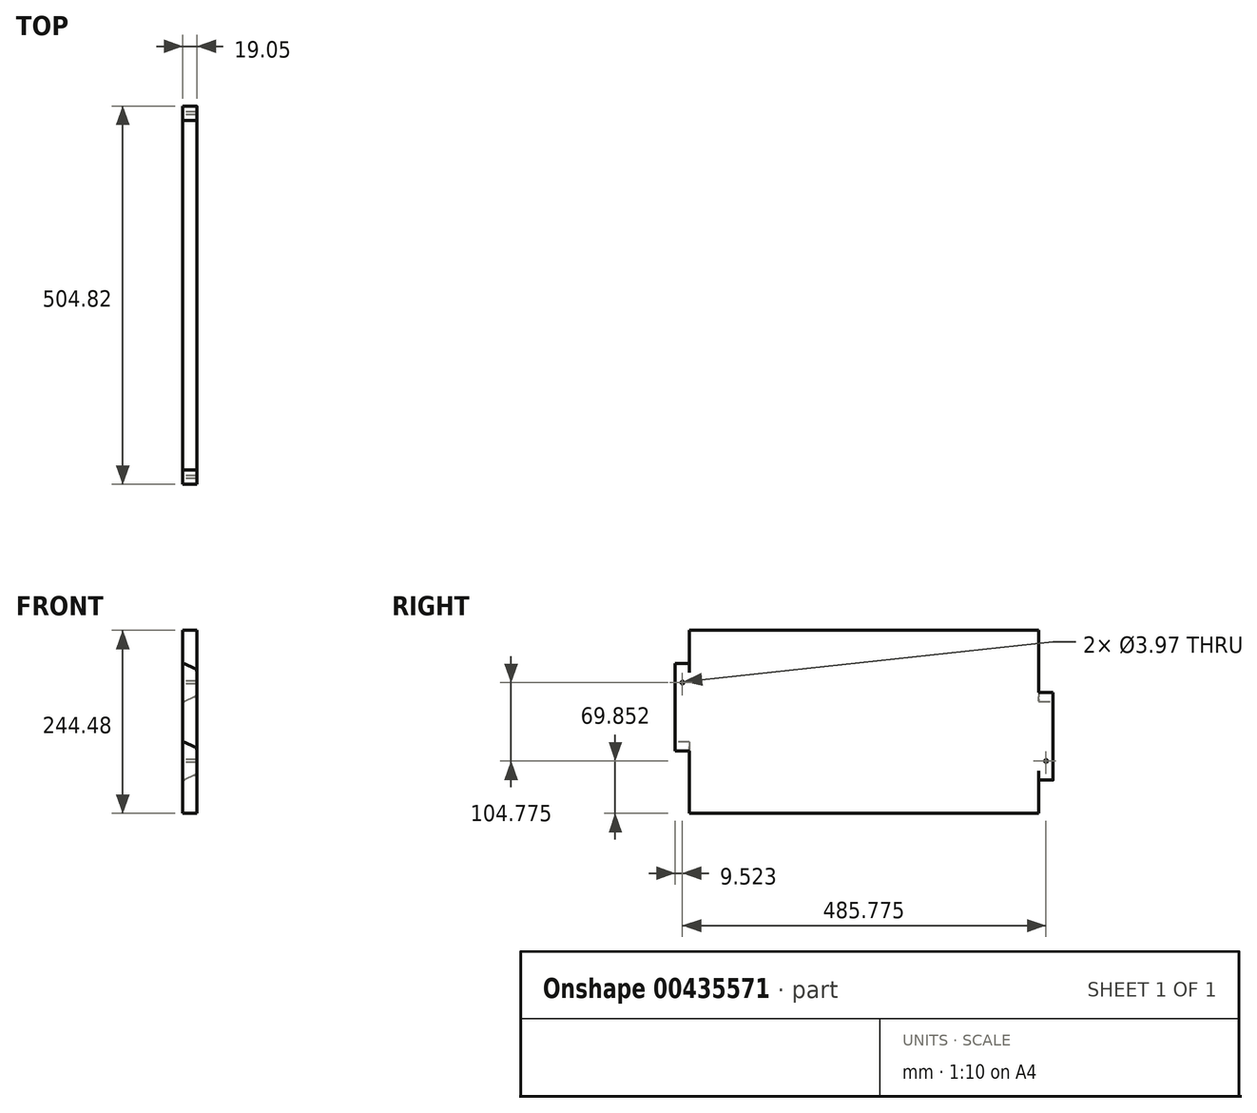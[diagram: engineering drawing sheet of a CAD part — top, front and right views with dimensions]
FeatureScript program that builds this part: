
annotation { "Feature Type Name" : "Feature", "Feature Type Description" : "" }
export const myFeature = defineFeature(function(context is Context, id is Id, definition is map)
    precondition{}
    {
        {
            var Q0;
            Q0=qCreatedBy(makeId("Right.planeOp"),FACE);
            var sketch = newSketch(context, id + "F0", { "sketchPlane" : qUnion([Q0])});
            skLineSegment(sketch, "E0.bottom", {"start": v(252.41, 122.24) * mm, "end": v(-252.41, 122.24) * mm});
            skLineSegment(sketch, "E0.top", {"start": v(252.41, -122.24) * mm, "end": v(-252.41, -122.24) * mm});
            skLineSegment(sketch, "E0.left", {"start": v(252.41, 122.24) * mm, "end": v(252.41, -122.24) * mm});
            skLineSegment(sketch, "E0.right", {"start": v(-252.41, 122.24) * mm, "end": v(-252.41, -122.24) * mm});
            skPoint(sketch, "E0.middle", {"position": v(0, 0) * mm});
            skSolve(sketch);
        }
        {
            var Q0;
            Q0=makeQuery(id+"F0.imprint","IMPRINT",FACE,{"disambiguationData":[TD([[makeQuery(id+"F0.imprint","IMPRINT",EDGE,{"derivedFrom":sQuery(id+"F0.wireOp",EDGE,"E0.bottom")}),1.0]])]});
            extrude(context, id + "F1", {"entities" : qUnion([Q0]), "depth" : 19.05 * mm, "offsetDistance" : 25.4 * mm});
        }
        {
            var Q0;
            Q0=makeQuery(id+"F1.opExtrude","SWEPT_FACE",FACE,{"disambiguationData":[OSD([sQuery(id+"F0.wireOp",EDGE,"E0.right")])]});
            var sketch = newSketch(context, id + "F2", { "sketchPlane" : qUnion([Q0])});
            skLineSegment(sketch, "E1", {"start": v(0, -122.24) * mm, "end": v(0, 122.24) * mm});
            skArc(sketch, "E2.MirrorCS", {"start": v(0.21, -26.99) * mm, "mid": v(1.56, -27.13) * mm, "end": v(2.84, -27.56) * mm});
            skLineSegment(sketch, "E3.MirrorCS", {"start": v(0.21, -77.79) * mm, "end": v(0, -77.79) * mm});
            skArc(sketch, "E4.MirrorCS", {"start": v(2.84, -77.22) * mm, "mid": v(1.56, -77.64) * mm, "end": v(0.21, -77.79) * mm});
            skLineSegment(sketch, "E5.MirrorCS", {"start": v(0, -26.99) * mm, "end": v(0.21, -26.99) * mm});
            skLineSegment(sketch, "E6.MirrorCS", {"start": v(15.33, -71.54) * mm, "end": v(2.84, -77.22) * mm});
            skArc(sketch, "E7.MirrorCS", {"start": v(15.33, -33.23) * mm, "mid": v(18.04, -35.58) * mm, "end": v(19.05, -39.01) * mm});
            skArc(sketch, "E8.MirrorCS", {"start": v(19.05, -65.76) * mm, "mid": v(18.04, -69.2) * mm, "end": v(15.33, -71.54) * mm});
            skLineSegment(sketch, "E9.MirrorCS", {"start": v(19.05, -39.01) * mm, "end": v(19.05, -65.76) * mm});
            skLineSegment(sketch, "E10.MirrorCS", {"start": v(2.84, -27.56) * mm, "end": v(15.33, -33.23) * mm});
            skPoint(sketch, "E11.MirrorP", {"position": v(1.59, -77.79) * mm});
            skPoint(sketch, "E12.MirrorP", {"position": v(19.05, -34.93) * mm});
            skPoint(sketch, "E13.MirrorP", {"position": v(1.59, -26.99) * mm});
            skPoint(sketch, "E14.MirrorP", {"position": v(19.05, -69.85) * mm});
            skLineSegment(sketch, "E15.MirrorCS", {"start": v(0.21, 77.79) * mm, "end": v(0, 77.79) * mm});
            skArc(sketch, "E16.MirrorCS", {"start": v(0.21, 26.99) * mm, "mid": v(1.56, 27.13) * mm, "end": v(2.84, 27.56) * mm});
            skLineSegment(sketch, "E17.MirrorCS", {"start": v(0, 26.99) * mm, "end": v(0.21, 26.99) * mm});
            skArc(sketch, "E18.MirrorCS", {"start": v(2.84, 77.22) * mm, "mid": v(1.56, 77.64) * mm, "end": v(0.21, 77.79) * mm});
            skLineSegment(sketch, "E19.MirrorCS", {"start": v(15.33, 71.54) * mm, "end": v(2.84, 77.22) * mm});
            skArc(sketch, "E20.MirrorCS", {"start": v(15.33, 33.23) * mm, "mid": v(18.04, 35.58) * mm, "end": v(19.05, 39.01) * mm});
            skArc(sketch, "E21.MirrorCS", {"start": v(19.05, 65.76) * mm, "mid": v(18.04, 69.2) * mm, "end": v(15.33, 71.54) * mm});
            skLineSegment(sketch, "E22.MirrorCS", {"start": v(2.84, 27.56) * mm, "end": v(15.33, 33.23) * mm});
            skLineSegment(sketch, "E23.MirrorCS", {"start": v(25.44, 66.94) * mm, "end": v(-6.35, 81.4) * mm, "construction": true});
            skLineSegment(sketch, "E24.MirrorCS", {"start": v(-6.35, 26.99) * mm, "end": v(9.53, 26.99) * mm, "construction": true});
            skLineSegment(sketch, "E25.MirrorCS", {"start": v(9.53, 77.79) * mm, "end": v(-6.35, 77.79) * mm, "construction": true});
            skLineSegment(sketch, "E26.MirrorCS", {"start": v(-6.35, 23.38) * mm, "end": v(25.44, 37.83) * mm, "construction": true});
            skLineSegment(sketch, "E27.MirrorCS", {"start": v(19.05, 39.01) * mm, "end": v(19.05, 65.76) * mm});
            skLineSegment(sketch, "E28.MirrorCS", {"start": v(19.05, 26.99) * mm, "end": v(19.05, 77.79) * mm, "construction": true});
            skPoint(sketch, "E29.MirrorP", {"position": v(1.59, 77.79) * mm});
            skPoint(sketch, "E30.MirrorP", {"position": v(19.05, 34.93) * mm});
            skPoint(sketch, "E31.MirrorP", {"position": v(1.59, 26.99) * mm});
            skLineSegment(sketch, "E32.MirrorCS", {"start": v(0, 20.64) * mm, "end": v(0, 84.14) * mm, "construction": true});
            skPoint(sketch, "E33.MirrorP", {"position": v(19.05, 69.85) * mm});
            skSolve(sketch);
        }
        {
            var Q0;
            Q0=makeQuery(id+"F1.opExtrude","SWEPT_FACE",FACE,{"disambiguationData":[OSD([sQuery(id+"F0.wireOp",EDGE,"E0.left")])]});
            var sketch = newSketch(context, id + "F3", { "sketchPlane" : qUnion([Q0])});
            skLineSegment(sketch, "E34", {"start": v(0, 122.24) * mm, "end": v(0, -122.24) * mm});
            skArc(sketch, "E35.MirrorCS", {"start": v(-0.21, 26.99) * mm, "mid": v(-1.56, 27.13) * mm, "end": v(-2.84, 27.56) * mm});
            skLineSegment(sketch, "E36.MirrorCS", {"start": v(-0.21, 77.79) * mm, "end": v(0, 77.79) * mm});
            skArc(sketch, "E37.MirrorCS", {"start": v(-2.84, 77.22) * mm, "mid": v(-1.56, 77.64) * mm, "end": v(-0.21, 77.79) * mm});
            skLineSegment(sketch, "E38.MirrorCS", {"start": v(0, 26.99) * mm, "end": v(-0.21, 26.99) * mm});
            skLineSegment(sketch, "E39.MirrorCS", {"start": v(-15.33, 71.54) * mm, "end": v(-2.84, 77.22) * mm});
            skArc(sketch, "E40.MirrorCS", {"start": v(-15.33, 33.23) * mm, "mid": v(-18.04, 35.58) * mm, "end": v(-19.05, 39.01) * mm});
            skArc(sketch, "E41.MirrorCS", {"start": v(-19.05, 65.76) * mm, "mid": v(-18.04, 69.2) * mm, "end": v(-15.33, 71.54) * mm});
            skLineSegment(sketch, "E42.MirrorCS", {"start": v(-19.05, 39.01) * mm, "end": v(-19.05, 65.76) * mm});
            skLineSegment(sketch, "E43.MirrorCS", {"start": v(-2.84, 27.56) * mm, "end": v(-15.33, 33.23) * mm});
            skPoint(sketch, "E44.MirrorP", {"position": v(-1.59, 77.79) * mm});
            skPoint(sketch, "E45.MirrorP", {"position": v(-19.05, 34.93) * mm});
            skPoint(sketch, "E46.MirrorP", {"position": v(-1.59, 26.99) * mm});
            skPoint(sketch, "E47.MirrorP", {"position": v(-19.05, 69.85) * mm});
            skLineSegment(sketch, "E48.MirrorCS", {"start": v(-0.21, -77.79) * mm, "end": v(0, -77.79) * mm});
            skArc(sketch, "E49.MirrorCS", {"start": v(-0.21, -26.99) * mm, "mid": v(-1.56, -27.13) * mm, "end": v(-2.84, -27.56) * mm});
            skLineSegment(sketch, "E50.MirrorCS", {"start": v(0, -26.99) * mm, "end": v(-0.21, -26.99) * mm});
            skArc(sketch, "E51.MirrorCS", {"start": v(-2.84, -77.22) * mm, "mid": v(-1.56, -77.64) * mm, "end": v(-0.21, -77.79) * mm});
            skLineSegment(sketch, "E52.MirrorCS", {"start": v(-15.33, -71.54) * mm, "end": v(-2.84, -77.22) * mm});
            skArc(sketch, "E53.MirrorCS", {"start": v(-15.33, -33.23) * mm, "mid": v(-18.04, -35.58) * mm, "end": v(-19.05, -39.01) * mm});
            skArc(sketch, "E54.MirrorCS", {"start": v(-19.05, -65.76) * mm, "mid": v(-18.04, -69.2) * mm, "end": v(-15.33, -71.54) * mm});
            skLineSegment(sketch, "E55.MirrorCS", {"start": v(-2.84, -27.56) * mm, "end": v(-15.33, -33.23) * mm});
            skLineSegment(sketch, "E56.MirrorCS", {"start": v(-25.44, -66.94) * mm, "end": v(6.35, -81.4) * mm, "construction": true});
            skLineSegment(sketch, "E57.MirrorCS", {"start": v(6.35, -26.99) * mm, "end": v(-9.53, -26.99) * mm, "construction": true});
            skLineSegment(sketch, "E58.MirrorCS", {"start": v(-9.53, -77.79) * mm, "end": v(6.35, -77.79) * mm, "construction": true});
            skLineSegment(sketch, "E59.MirrorCS", {"start": v(6.35, -23.38) * mm, "end": v(-25.44, -37.83) * mm, "construction": true});
            skLineSegment(sketch, "E60.MirrorCS", {"start": v(-19.05, -39.01) * mm, "end": v(-19.05, -65.76) * mm});
            skLineSegment(sketch, "E61.MirrorCS", {"start": v(-19.05, -26.99) * mm, "end": v(-19.05, -77.79) * mm, "construction": true});
            skPoint(sketch, "E62.MirrorP", {"position": v(-1.59, -77.79) * mm});
            skPoint(sketch, "E63.MirrorP", {"position": v(-19.05, -34.93) * mm});
            skPoint(sketch, "E64.MirrorP", {"position": v(-1.59, -26.99) * mm});
            skLineSegment(sketch, "E65.MirrorCS", {"start": v(0, -20.64) * mm, "end": v(0, -84.14) * mm, "construction": true});
            skPoint(sketch, "E66.MirrorP", {"position": v(-19.05, -69.85) * mm});
            skSolve(sketch);
        }
        {
            var Q0;
            {var subQ0=sQuery(id+"F3.wireOp",EDGE,"E36.MirrorCS");Q0=makeQuery(id+"F3.imprint","IMPRINT",FACE,{"disambiguationData":[TD([[makeQuery(id+"F3.imprint","IMPRINT",EDGE,{"derivedFrom":subQ0}),1.0]])]});}
            var Q1;
            Q1=makeQuery(id+"F3.imprint","IMPRINT",FACE,{"disambiguationData":[TD([[makeQuery(id+"F3.imprint","IMPRINT",EDGE,{"derivedFrom":sQuery(id+"F3.wireOp",EDGE,"E35.MirrorCS")}),1.0]])]});
            var Q2;
            {var subQ0=sQuery(id+"F3.wireOp",EDGE,"E48.MirrorCS");Q2=makeQuery(id+"F3.imprint","IMPRINT",FACE,{"disambiguationData":[TD([[makeQuery(id+"F3.imprint","IMPRINT",EDGE,{"derivedFrom":subQ0}),-1.0]])]});}
            extrude(context, id + "F4", {"entities" : qUnion([Q0, Q1, Q2]), "operationType" : NewBodyOperationType.REMOVE, "oppositeDirection" : true, "depth" : 19.05 * mm, "offsetDistance" : 25.4 * mm});
        }
        {
            var Q0;
            {var subQ0=sQuery(id+"F2.wireOp",EDGE,"E15.MirrorCS");Q0=makeQuery(id+"F2.imprint","IMPRINT",FACE,{"disambiguationData":[TD([[makeQuery(id+"F2.imprint","IMPRINT",EDGE,{"derivedFrom":subQ0}),-1.0]])]});}
            var Q1;
            Q1=makeQuery(id+"F2.imprint","IMPRINT",FACE,{"disambiguationData":[TD([[makeQuery(id+"F2.imprint","IMPRINT",EDGE,{"derivedFrom":sQuery(id+"F2.wireOp",EDGE,"E2.MirrorCS")}),1.0]])]});
            var Q2;
            {var subQ0=sQuery(id+"F2.wireOp",EDGE,"E3.MirrorCS");Q2=makeQuery(id+"F2.imprint","IMPRINT",FACE,{"disambiguationData":[TD([[makeQuery(id+"F2.imprint","IMPRINT",EDGE,{"derivedFrom":subQ0}),1.0]])]});}
            extrude(context, id + "F5", {"entities" : qUnion([Q0, Q1, Q2]), "operationType" : NewBodyOperationType.REMOVE, "oppositeDirection" : true, "depth" : 19.05 * mm, "offsetDistance" : 25.4 * mm});
        }
        {
            var Q0;
            Q0=makeQuery(id+"F1.opExtrude","CAP_FACE",FACE,{"disambiguationData":[OSD([sQuery(id+"F0.wireOp",EDGE,"E0.bottom"),sQuery(id+"F0.wireOp",EDGE,"E0.top"),sQuery(id+"F0.wireOp",EDGE,"E0.left"),sQuery(id+"F0.wireOp",EDGE,"E0.right")])],"isStart":true});
            var sketch = newSketch(context, id + "F6", { "sketchPlane" : qUnion([Q0])});
            skCircle(sketch, "E67", {"center": v(-242.89, 52.39) * mm, "radius": 1.98 * mm});
            skPoint(sketch, "E67.centerSnap0", {"position": v(-242.89, 26.99) * mm});
            skPoint(sketch, "E67.centerSnap1", {"position": v(-252.41, 52.39) * mm});
            skCircle(sketch, "E68", {"center": v(-242.89, -52.39) * mm, "radius": 1.98 * mm});
            skPoint(sketch, "E69", {"position": v(-242.89, -77.79) * mm});
            skPoint(sketch, "E70", {"position": v(-252.41, -52.39) * mm});
            skCircle(sketch, "E71", {"center": v(242.89, 52.39) * mm, "radius": 1.98 * mm});
            skCircle(sketch, "E72", {"center": v(242.89, -52.39) * mm, "radius": 1.98 * mm});
            skPoint(sketch, "E73", {"position": v(242.89, -77.79) * mm});
            skPoint(sketch, "E74", {"position": v(252.41, -52.39) * mm});
            skSolve(sketch);
        }
        {
            var Q0;
            Q0=makeQuery(id+"F6.imprint","IMPRINT",FACE,{"disambiguationData":[TD([[makeQuery(id+"F6.imprint","IMPRINT",EDGE,{"derivedFrom":sQuery(id+"F6.wireOp",EDGE,"E68")}),1.0]])]});
            var Q1;
            Q1=makeQuery(id+"F6.imprint","IMPRINT",FACE,{"disambiguationData":[TD([[makeQuery(id+"F6.imprint","IMPRINT",EDGE,{"derivedFrom":sQuery(id+"F6.wireOp",EDGE,"E67")}),1.0]])]});
            var Q2;
            Q2=makeQuery(id+"F6.imprint","IMPRINT",FACE,{"disambiguationData":[TD([[makeQuery(id+"F6.imprint","IMPRINT",EDGE,{"derivedFrom":sQuery(id+"F6.wireOp",EDGE,"E71")}),1.0]])]});
            var Q3;
            Q3=makeQuery(id+"F6.imprint","IMPRINT",FACE,{"disambiguationData":[TD([[makeQuery(id+"F6.imprint","IMPRINT",EDGE,{"derivedFrom":sQuery(id+"F6.wireOp",EDGE,"E72")}),1.0]])]});
            extrude(context, id + "F7", {"entities" : qUnion([Q0, Q1, Q2, Q3]), "operationType" : NewBodyOperationType.REMOVE, "oppositeDirection" : true, "depth" : 19.05 * mm, "offsetDistance" : 25.4 * mm});
        }
    });
